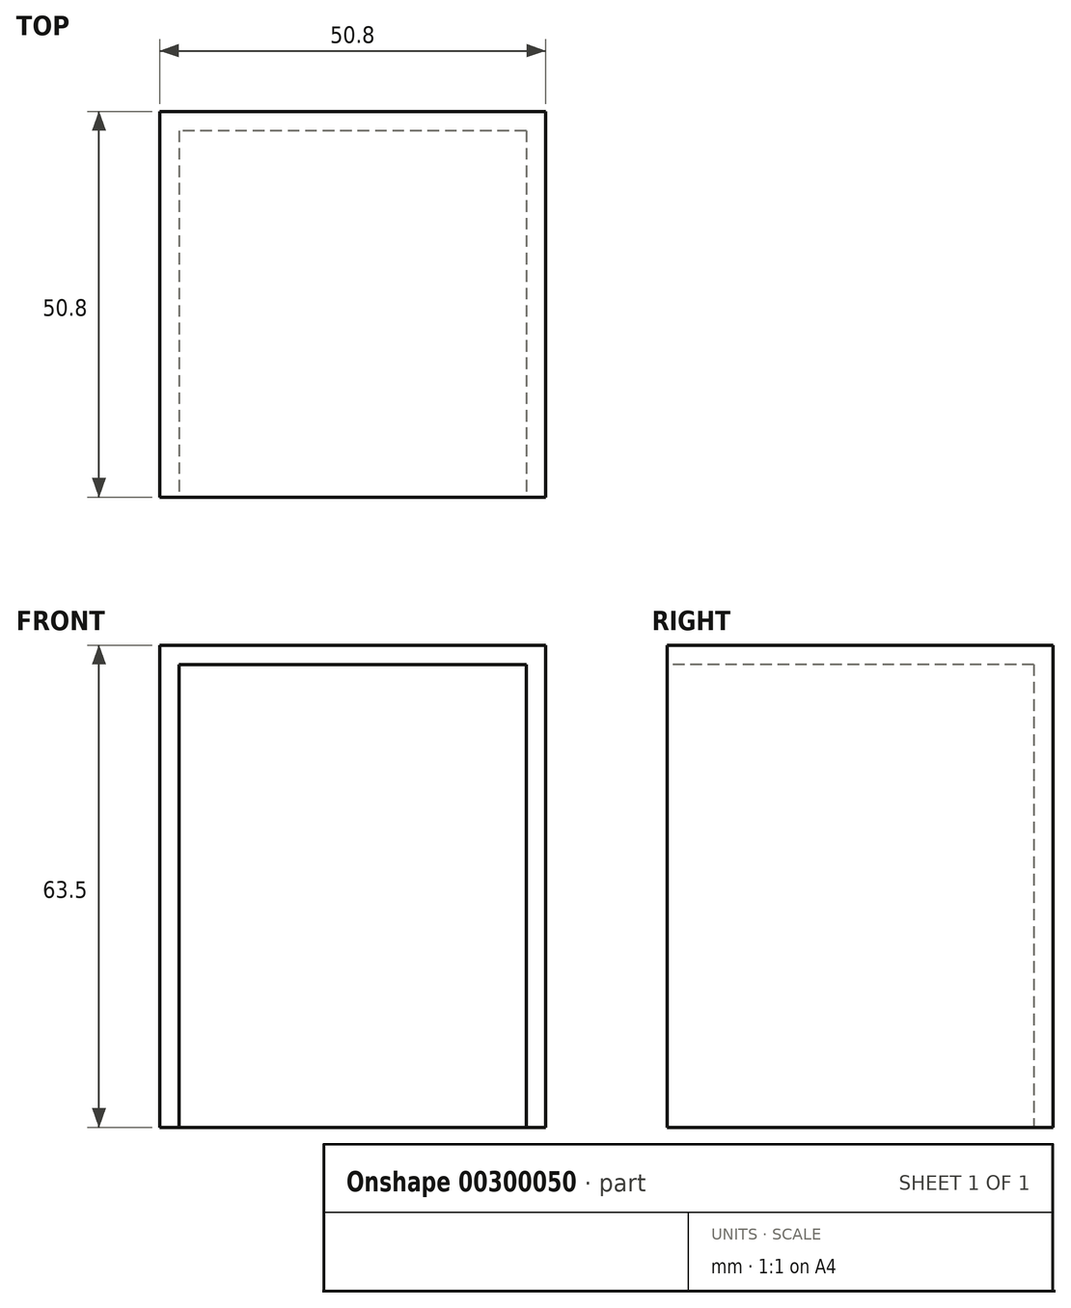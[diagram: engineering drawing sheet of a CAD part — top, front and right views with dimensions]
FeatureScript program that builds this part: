
annotation { "Feature Type Name" : "Feature", "Feature Type Description" : "" }
export const myFeature = defineFeature(function(context is Context, id is Id, definition is map)
    precondition{}
    {
        {
            var Q0;
            Q0=qCreatedBy(makeId("Top.planeOp"),FACE);
            var sketch = newSketch(context, id + "F0", { "sketchPlane" : qUnion([Q0])});
            skLineSegment(sketch, "E0.bottom", {"start": v(25.4, 25.4) * mm, "end": v(-25.4, 25.4) * mm});
            skLineSegment(sketch, "E0.top", {"start": v(25.4, -25.4) * mm, "end": v(-25.4, -25.4) * mm});
            skLineSegment(sketch, "E0.left", {"start": v(25.4, 25.4) * mm, "end": v(25.4, -25.4) * mm});
            skLineSegment(sketch, "E0.right", {"start": v(-25.4, 25.4) * mm, "end": v(-25.4, -25.4) * mm});
            skPoint(sketch, "E0.middle", {"position": v(0, 0) * mm});
            skSolve(sketch);
        }
        {
            var Q0;
            Q0 = qSketchRegion(id + "F0", true);
            extrude(context, id + "F1", {"entities" : qUnion([Q0]), "endBound" : BoundingType.SYMMETRIC, "depth" : 63.5 * mm});
        }
        {
            var Q0;
            Q0=makeQuery(id+"F1.opExtrude","CAP_FACE",FACE,{"disambiguationData":[OSD([sQuery(id+"F0.wireOp",EDGE,"E0.bottom"),sQuery(id+"F0.wireOp",EDGE,"E0.top"),sQuery(id+"F0.wireOp",EDGE,"E0.left"),sQuery(id+"F0.wireOp",EDGE,"E0.right")])],"isStart":true});
            shell(context, id + "F2", {"entities" : qUnion([Q0]), "thickness" : 2.54 * mm});
        }
        {
            var Q0;
            Q0=qCreatedBy(makeId("Front.planeOp"),FACE);
            var sketch = newSketch(context, id + "F3", { "sketchPlane" : qUnion([Q0])});
            skLineSegment(sketch, "E1", {"start": v(0, 50.6) * mm, "end": v(0, -51.34) * mm, "construction": true});
            skSolve(sketch);
        }
        {
            var Q0;
            Q0=makeQuery(id+"F1.opExtrude","SWEPT_FACE",FACE,{"disambiguationData":[OSD([sQuery(id+"F0.wireOp",EDGE,"E0.top")])]});
            var sketch = newSketch(context, id + "F4", { "sketchPlane" : qUnion([Q0])});
            skLineSegment(sketch, "E2.bottom", {"start": v(-22.86, -31.75) * mm, "end": v(22.86, -31.75) * mm});
            skLineSegment(sketch, "E2.top", {"start": v(-22.86, 29.21) * mm, "end": v(22.86, 29.21) * mm});
            skLineSegment(sketch, "E2.left", {"start": v(-22.86, -31.75) * mm, "end": v(-22.86, 29.21) * mm});
            skLineSegment(sketch, "E2.right", {"start": v(22.86, -31.75) * mm, "end": v(22.86, 29.21) * mm});
            skSolve(sketch);
        }
        {
            var Q0;
            Q0 = qSketchRegion(id + "F4", true);
            extrude(context, id + "F5", {"entities" : qUnion([Q0]), "operationType" : NewBodyOperationType.REMOVE, "endBound" : BoundingType.UP_TO_NEXT, "oppositeDirection" : true, "depth" : 25.4 * mm});
        }
    });
